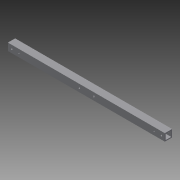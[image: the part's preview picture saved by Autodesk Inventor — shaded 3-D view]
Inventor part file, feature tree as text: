
AUTODESK INVENTOR PART (.ipt)
format: ipt  version: 2015 SP1 (Build 190203100, 203)  size: 160,256 bytes
history: native  units: in
note: dims shown in document units (in); Inventor stores cm internally (conversion verified against a paired STEP export)
features: sketch x7, extrude x4, hole x3, projected_geometry x3
ambient origin geometry x8: Origin, YZ Plane, XZ Plane, XY Plane, X Axis, Y Axis, Z Axis, Center Point
bodies: Solid1 (feature_tree)
feature tree (17):
  extrude  "Extrusion1"  Depth=1.0in
  hole  "Hole1"  [1 undecoded]
  hole  "Hole2"  [1 undecoded]
  hole  "Hole3"  [1 undecoded]
  extrude  "Extrusion2"  Depth=0.5in
  extrude  "Extrusion3"  Depth=1.0in
  extrude  "Extrusion4"  Depth=1.0in
  sketch  "Sketch1"  dims[d0=1.0in d1=1.0in]
  sketch  "Sketch2"  dims[d2=0.75in d3=0.75in]
  projected_geometry  "Projected Loop1"
  sketch  "Sketch3"  dims[d4=0.125in d5=0.125in]
  projected_geometry  "Projected Loop2"
  sketch  "Sketch4"  dims[d6=21.5in d7=0.0in d8=0.5in]
  projected_geometry  "Projected Loop3"
  sketch  "Sketch7"  dims[d9=0.5in d10=0.5in]
  sketch  "Sketch8"  dims[d11=0.5in]
  sketch  "Sketch9"  dims[d12=0.25in d13=0.75in d14=0.375in d15=0.25in d16=0.5635in d17=1.0in d18=0.8108in d19=9.75in d20=9.75in d21=0.5in d22=0.5in d23=0.25in d24=0.75in d25=0.375in d26=0.25in d27=0.5635in d28=1.0in d29=0.8108in d30=1.5in d31=0.5in d32=0.5in d33=1.5in d34=0.1875in d35=0.75in d36=0.375in d37=0.25in d38=0.5635in d39=1.0in d40=0.8108in d65=0.25in d66=0.25in d67=0.5in d68=1.0in d69=0.25in d70=0.25in d71=0.5in d72=1.0in d73=1.0in d74=0.0in d75=1.0in d76=0.0in d77=1.0in d78=0.0in]
note: 3 required parameter values undecoded (feature->parameter linkage not recoverable at this tier; creation-order binding heuristic only, values carry confidence <= 0.55)
